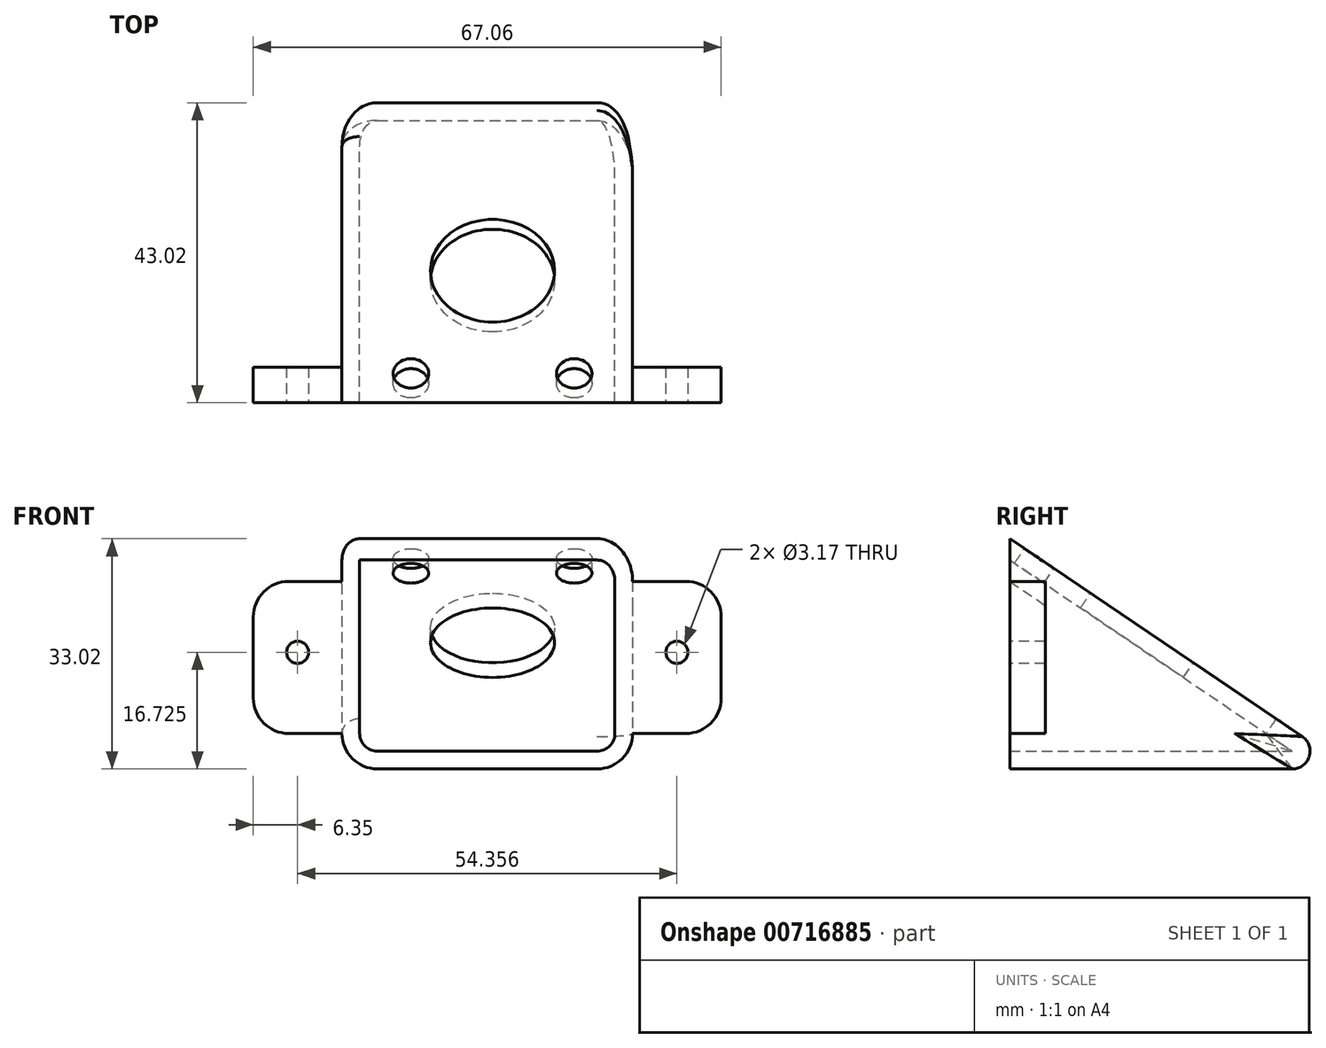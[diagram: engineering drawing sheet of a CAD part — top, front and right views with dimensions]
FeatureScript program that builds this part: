
annotation { "Feature Type Name" : "Feature", "Feature Type Description" : "" }
export const myFeature = defineFeature(function(context is Context, id is Id, definition is map)
    precondition{}
    {
        {
            var Q0;
            Q0=qCreatedBy(makeId("Top.planeOp"),FACE);
            var sketch = newSketch(context, id + "F0", { "sketchPlane" : qUnion([Q0])});
            skLineSegment(sketch, "E0.bottom", {"start": v(-40.64, 54.85) * mm, "end": v(1.02, 54.85) * mm});
            skLineSegment(sketch, "E0.top", {"start": v(-40.64, 6.08) * mm, "end": v(1.02, 6.08) * mm});
            skLineSegment(sketch, "E0.left", {"start": v(-40.64, 54.85) * mm, "end": v(-40.64, 6.08) * mm});
            skLineSegment(sketch, "E0.right", {"start": v(1.02, 54.85) * mm, "end": v(1.02, 6.08) * mm});
            skSolve(sketch);
        }
        {
            var Q0;
            Q0=makeQuery(id+"F0.imprint","IMPRINT",FACE,{"disambiguationData":[TD([[makeQuery(id+"F0.imprint","IMPRINT",EDGE,{"derivedFrom":sQuery(id+"F0.wireOp",EDGE,"E0.bottom")}),-1.0]])]});
            extrude(context, id + "F1", {"entities" : qUnion([Q0]), "depth" : 33.02 * mm, "offsetDistance" : 25.4 * mm});
        }
        {
            var Q0;
            Q0=makeQuery(id+"F1.opExtrude","SWEPT_FACE",FACE,{"disambiguationData":[OSD([sQuery(id+"F0.wireOp",EDGE,"E0.left")])]});
            var sketch = newSketch(context, id + "F2", { "sketchPlane" : qUnion([Q0])});
            skLineSegment(sketch, "E1", {"start": v(-54.85, 0) * mm, "end": v(-6.08, 33.02) * mm});
            skSolve(sketch);
        }
        {
            var Q0;
            Q0=makeQuery(id+"F2.imprint","IMPRINT",FACE,{"disambiguationData":[TD([[makeQuery(id+"F2.imprint","IMPRINT",EDGE,{"derivedFrom":sQuery(id+"F2.wireOp",EDGE,"E1")}),1.0]])]});
            extrude(context, id + "F3", {"entities" : qUnion([Q0]), "operationType" : NewBodyOperationType.REMOVE, "oppositeDirection" : true, "depth" : 90.17 * mm, "offsetDistance" : 25.4 * mm});
        }
        {
            var Q0;
            Q0=makeQuery(id+"F1.opExtrude","CAP_EDGE",EDGE,{"disambiguationData":[OSD([sQuery(id+"F0.wireOp",EDGE,"E0.right")])],"isStart":true});
            var Q1;
            Q1=makeQuery(id+"F3.boolean.opBoolean","INTERSECT",EDGE,{"derivedFrom":[makeQuery(id+"F1.opExtrude","SWEPT_FACE",FACE,{"disambiguationData":[OSD([sQuery(id+"F0.wireOp",EDGE,"E0.right")])]}),makeQuery(id+"F3.opExtrude","SWEPT_FACE",FACE,{"disambiguationData":[OSD([sQuery(id+"F2.wireOp",EDGE,"E1")])]})]});
            var Q2;
            Q2=makeQuery(id+"F3.boolean.opBoolean","COPY",EDGE,{"derivedFrom":makeQuery(id+"F3.opExtrude","CAP_EDGE",EDGE,{"disambiguationData":[OSD([sQuery(id+"F2.wireOp",EDGE,"E1")])],"isStart":true})});
            var Q3;
            Q3=makeQuery(id+"F1.opExtrude","CAP_EDGE",EDGE,{"disambiguationData":[OSD([sQuery(id+"F0.wireOp",EDGE,"E0.left")])],"isStart":true});
            fillet(context, id + "F4", {"entities" : qUnion([Q0, Q1, Q2, Q3]), "radius" : 5.08 * mm, "tangentPropagation" : true, "allowEdgeOverflow" : false});
        }
        {
            var Q0;
            {var subQ0=sQuery(id+"F0.wireOp",EDGE,"E0.bottom");Q0=makeQuery(id+"F3.boolean.opBoolean","MERGE",EDGE,{"derivedFrom":[makeQuery(id+"F1.opExtrude","CAP_EDGE",EDGE,{"disambiguationData":[OSD([subQ0])],"isStart":true}),makeQuery(id+"F3.opExtrude","SWEPT_EDGE",EDGE,{"disambiguationData":[OSD([subQ0,sQuery(id+"F0.wireOp",EDGE,"E0.left"),sQuery(id+"F2.wireOp",EDGE,"E1")])]})]});}
            fillet(context, id + "F5", {"entities" : qUnion([Q0]), "radius" : 2.54 * mm, "tangentPropagation" : true, "allowEdgeOverflow" : false});
        }
        {
            var Q0;
            Q0=makeQuery(id+"F3.boolean.opBoolean","COPY",FACE,{"derivedFrom":makeQuery(id+"F3.opExtrude","SWEPT_FACE",FACE,{"disambiguationData":[OSD([sQuery(id+"F2.wireOp",EDGE,"E1")])]})});
            var sketch = newSketch(context, id + "F6", { "sketchPlane" : qUnion([Q0])});
            skCircle(sketch, "E2", {"center": v(-30.76, -8.4) * mm, "radius": 2.54 * mm});
            skCircle(sketch, "E3", {"center": v(-7.35, -8.4) * mm, "radius": 2.54 * mm});
            skCircle(sketch, "E4", {"center": v(-19.05, 9.38) * mm, "radius": 8.9 * mm});
            skSolve(sketch);
        }
        {
            var Q0;
            Q0=makeQuery(id+"F1.opExtrude","SWEPT_FACE",FACE,{"disambiguationData":[OSD([sQuery(id+"F0.wireOp",EDGE,"E0.top")])]});
            shell(context, id + "F7", {"entities" : qUnion([Q0]), "thickness" : 2.54 * mm});
        }
        {
            var Q0;
            Q0=makeQuery(id+"F6.imprint","IMPRINT",FACE,{"disambiguationData":[TD([[makeQuery(id+"F6.imprint","IMPRINT",EDGE,{"derivedFrom":sQuery(id+"F6.wireOp",EDGE,"E2")}),1.0]])]});
            var Q1;
            Q1=makeQuery(id+"F6.imprint","IMPRINT",FACE,{"disambiguationData":[TD([[makeQuery(id+"F6.imprint","IMPRINT",EDGE,{"derivedFrom":sQuery(id+"F6.wireOp",EDGE,"E4")}),1.0]])]});
            var Q2;
            Q2=makeQuery(id+"F6.imprint","IMPRINT",FACE,{"disambiguationData":[TD([[makeQuery(id+"F6.imprint","IMPRINT",EDGE,{"derivedFrom":sQuery(id+"F6.wireOp",EDGE,"E3")}),1.0]])]});
            var Q3;
            Q3=sQuery(id+"F6.wireOp",EDGE,"E4");
            var Q4;
            Q4=sQuery(id+"F6.wireOp",EDGE,"E2");
            var Q5;
            Q5=sQuery(id+"F6.wireOp",EDGE,"E3");
            extrude(context, id + "F8", {"entities" : qUnion([Q0, Q1, Q2]), "operationType" : NewBodyOperationType.REMOVE, "surfaceEntities" : qUnion([Q3, Q4, Q5]), "oppositeDirection" : true, "depth" : 1.42 * mm, "offsetDistance" : 25.4 * mm});
        }
        {
            var Q0;
            Q0=makeQuery(id+"F8.boolean.opBoolean","COPY",FACE,{"derivedFrom":makeQuery(id+"F8.opExtrude","CAP_FACE",FACE,{"disambiguationData":[OSD([sQuery(id+"F6.wireOp",EDGE,"E4")])],"isStart":false})});
            var Q1;
            Q1=makeQuery(id+"F8.boolean.opBoolean","COPY",FACE,{"derivedFrom":makeQuery(id+"F8.opExtrude","CAP_FACE",FACE,{"disambiguationData":[OSD([sQuery(id+"F6.wireOp",EDGE,"E2")])],"isStart":false})});
            var Q2;
            Q2=makeQuery(id+"F8.boolean.opBoolean","COPY",FACE,{"derivedFrom":makeQuery(id+"F8.opExtrude","CAP_FACE",FACE,{"disambiguationData":[OSD([sQuery(id+"F6.wireOp",EDGE,"E3")])],"isStart":false})});
            extrude(context, id + "F9", {"entities" : qUnion([Q0, Q1, Q2]), "operationType" : NewBodyOperationType.REMOVE, "oppositeDirection" : true, "depth" : 3.8 * mm, "offsetDistance" : 25.4 * mm});
        }
        {
            var Q0;
            Q0=makeQuery(id+"F1.opExtrude","SWEPT_FACE",FACE,{"disambiguationData":[OSD([sQuery(id+"F0.wireOp",EDGE,"E0.top")])]});
            var sketch = newSketch(context, id + "F10", { "sketchPlane" : qUnion([Q0])});
            skLineSegment(sketch, "E5.bottom", {"start": v(1.02, 26.89) * mm, "end": v(13.72, 26.89) * mm});
            skLineSegment(sketch, "E5.top", {"start": v(1.02, 5.08) * mm, "end": v(13.72, 5.08) * mm});
            skLineSegment(sketch, "E5.left", {"start": v(1.02, 26.89) * mm, "end": v(1.02, 5.08) * mm});
            skLineSegment(sketch, "E5.right", {"start": v(13.72, 26.89) * mm, "end": v(13.72, 5.08) * mm});
            skLineSegment(sketch, "E6.bottom", {"start": v(-40.64, 26.89) * mm, "end": v(-53.34, 26.89) * mm});
            skLineSegment(sketch, "E6.top", {"start": v(-40.64, 5.08) * mm, "end": v(-53.34, 5.08) * mm});
            skLineSegment(sketch, "E6.left", {"start": v(-40.64, 26.89) * mm, "end": v(-40.64, 5.08) * mm});
            skLineSegment(sketch, "E6.right", {"start": v(-53.34, 26.89) * mm, "end": v(-53.34, 5.08) * mm});
            skSolve(sketch);
        }
        {
            var Q0;
            Q0=makeQuery(id+"F10.imprint","IMPRINT",FACE,{"disambiguationData":[TD([[makeQuery(id+"F10.imprint","IMPRINT",EDGE,{"derivedFrom":sQuery(id+"F10.wireOp",EDGE,"E6.bottom")}),1.0]])]});
            var Q1;
            Q1=makeQuery(id+"F10.imprint","IMPRINT",FACE,{"disambiguationData":[TD([[makeQuery(id+"F10.imprint","IMPRINT",EDGE,{"derivedFrom":sQuery(id+"F10.wireOp",EDGE,"E5.bottom")}),-1.0]])]});
            extrude(context, id + "F11", {"entities" : qUnion([Q0, Q1]), "operationType" : NewBodyOperationType.ADD, "oppositeDirection" : true, "depth" : 5.08 * mm, "offsetDistance" : 25.4 * mm});
        }
        {
            var Q0;
            Q0=makeQuery(id+"F11.boolean.opBoolean","MERGE",FACE,{"derivedFrom":[makeQuery(id+"F1.opExtrude","SWEPT_FACE",FACE,{"disambiguationData":[OSD([sQuery(id+"F0.wireOp",EDGE,"E0.top")])]}),makeQuery(id+"F11.opExtrude","CAP_FACE",FACE,{"disambiguationData":[OSD([sQuery(id+"F10.wireOp",EDGE,"E5.bottom"),sQuery(id+"F10.wireOp",EDGE,"E5.top"),sQuery(id+"F10.wireOp",EDGE,"E5.left"),sQuery(id+"F10.wireOp",EDGE,"E5.right")])],"isStart":true}),makeQuery(id+"F11.opExtrude","CAP_FACE",FACE,{"disambiguationData":[OSD([sQuery(id+"F10.wireOp",EDGE,"E6.bottom"),sQuery(id+"F10.wireOp",EDGE,"E6.top"),sQuery(id+"F10.wireOp",EDGE,"E6.left"),sQuery(id+"F10.wireOp",EDGE,"E6.right")])],"isStart":true})]});
            var sketch = newSketch(context, id + "F12", { "sketchPlane" : qUnion([Q0])});
            skCircle(sketch, "E7", {"center": v(-46.99, 16.73) * mm, "radius": 1.59 * mm});
            skCircle(sketch, "E8", {"center": v(7.37, 16.73) * mm, "radius": 1.59 * mm});
            skSolve(sketch);
        }
        {
            var Q0;
            Q0=makeQuery(id+"F12.imprint","IMPRINT",FACE,{"disambiguationData":[TD([[makeQuery(id+"F12.imprint","IMPRINT",EDGE,{"derivedFrom":sQuery(id+"F12.wireOp",EDGE,"E7")}),1.0]])]});
            var Q1;
            Q1=makeQuery(id+"F12.imprint","IMPRINT",FACE,{"disambiguationData":[TD([[makeQuery(id+"F12.imprint","IMPRINT",EDGE,{"derivedFrom":sQuery(id+"F12.wireOp",EDGE,"E8")}),1.0]])]});
            var Q2;
            Q2=sQuery(id+"F12.wireOp",EDGE,"9ivVBFSL-sHKy-JtaL-dwiv-NxNFrRwKzWoG");
            extrude(context, id + "F13", {"entities" : qUnion([Q0, Q1]), "operationType" : NewBodyOperationType.REMOVE, "surfaceEntities" : qUnion([Q2]), "oppositeDirection" : true, "depth" : 5.08 * mm, "offsetDistance" : 25.4 * mm});
        }
        {
            var Q0;
            Q0=makeQuery(id+"F11.opExtrude","SWEPT_EDGE",EDGE,{"disambiguationData":[OSD([sQuery(id+"F10.wireOp",EDGE,"E6.bottom"),sQuery(id+"F10.wireOp",EDGE,"E6.right")])]});
            var Q1;
            Q1=makeQuery(id+"F11.opExtrude","SWEPT_EDGE",EDGE,{"disambiguationData":[OSD([sQuery(id+"F10.wireOp",EDGE,"E5.bottom"),sQuery(id+"F10.wireOp",EDGE,"E5.right")])]});
            var Q2;
            Q2=makeQuery(id+"F11.opExtrude","SWEPT_EDGE",EDGE,{"disambiguationData":[OSD([sQuery(id+"F10.wireOp",EDGE,"E6.top"),sQuery(id+"F10.wireOp",EDGE,"E6.right")])]});
            var Q3;
            Q3=makeQuery(id+"F11.opExtrude","SWEPT_EDGE",EDGE,{"disambiguationData":[OSD([sQuery(id+"F10.wireOp",EDGE,"E5.top"),sQuery(id+"F10.wireOp",EDGE,"E5.right")])]});
            fillet(context, id + "F14", {"entities" : qUnion([Q0, Q1, Q2, Q3]), "radius" : 5.08 * mm, "tangentPropagation" : true, "allowEdgeOverflow" : false});
        }
    });
